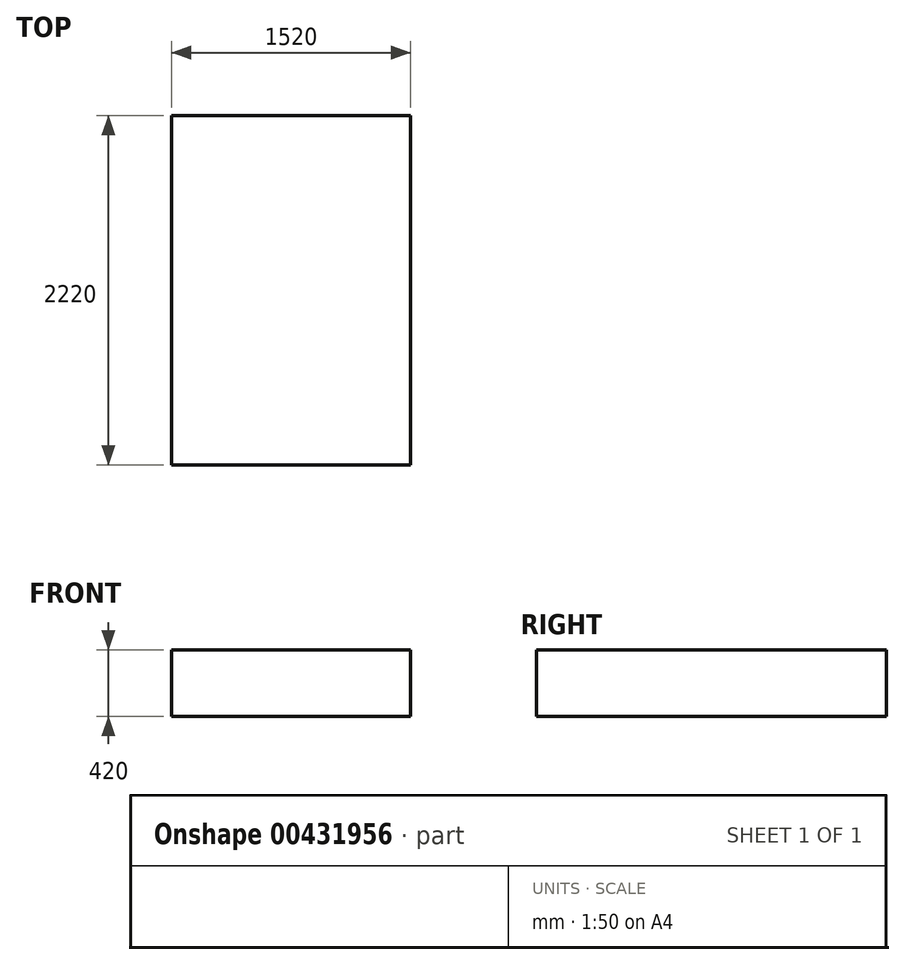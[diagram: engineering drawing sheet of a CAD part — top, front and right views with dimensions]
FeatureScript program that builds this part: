
annotation { "Feature Type Name" : "Feature", "Feature Type Description" : "" }
export const myFeature = defineFeature(function(context is Context, id is Id, definition is map)
    precondition{}
    {
        {
            var Q0;
            Q0=qCreatedBy(makeId("Top.planeOp"),FACE);
            var sketch = newSketch(context, id + "F0", { "sketchPlane" : qUnion([Q0])});
            skLineSegment(sketch, "E0.bottom", {"start": v(-760, 1110) * mm, "end": v(760, 1110) * mm});
            skLineSegment(sketch, "E0.top", {"start": v(-760, -1110) * mm, "end": v(760, -1110) * mm});
            skLineSegment(sketch, "E0.left", {"start": v(-760, 1110) * mm, "end": v(-760, -1110) * mm});
            skLineSegment(sketch, "E0.right", {"start": v(760, 1110) * mm, "end": v(760, -1110) * mm});
            skPoint(sketch, "E0.middle", {"position": v(0, 0) * mm});
            skSolve(sketch);
        }
        {
            var Q0;
            Q0 = qSketchRegion(id + "F0", true);
            extrude(context, id + "F1", {"entities" : qUnion([Q0]), "depth" : 420 * mm});
        }
    });
